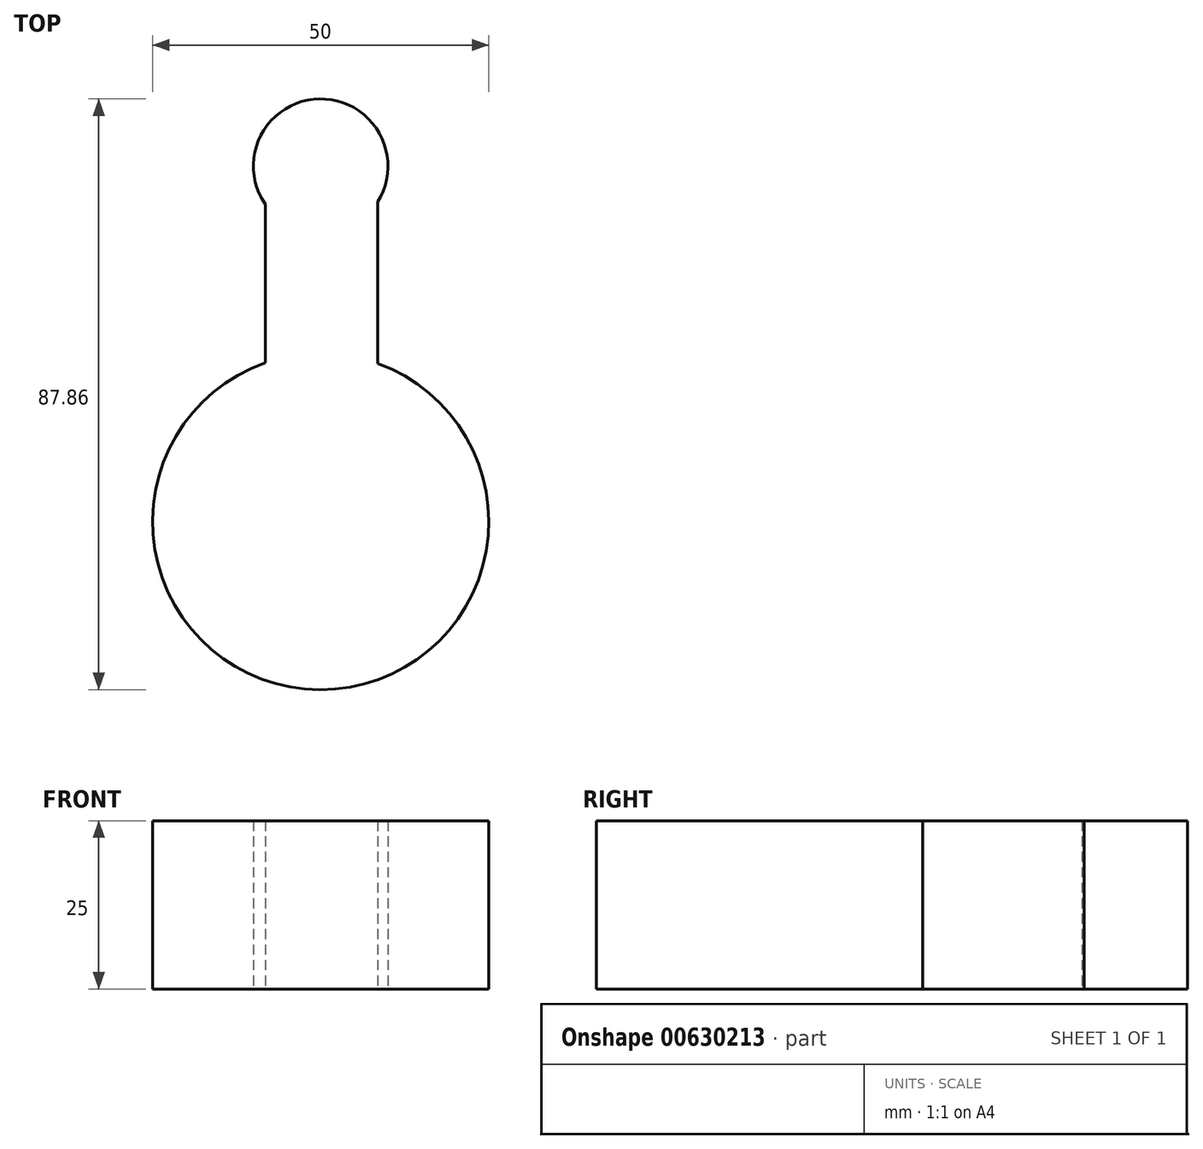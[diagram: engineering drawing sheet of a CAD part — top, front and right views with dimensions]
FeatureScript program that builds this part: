
annotation { "Feature Type Name" : "Feature", "Feature Type Description" : "" }
export const myFeature = defineFeature(function(context is Context, id is Id, definition is map)
    precondition{}
    {
        {
            var Q0;
            Q0=qCreatedBy(makeId("Top.planeOp"),FACE);
            var sketch = newSketch(context, id + "F0", { "sketchPlane" : qUnion([Q0])});
            skArc(sketch, "E0", {"start": v(-8.25, 23.6) * mm, "mid": v(-0.11, -25) * mm, "end": v(8.47, 23.52) * mm});
            skArc(sketch, "E1", {"start": v(8.47, 47.54) * mm, "mid": v(-0.2, 62.86) * mm, "end": v(-8.25, 47.21) * mm});
            skLineSegment(sketch, "E2", {"start": v(-8.25, 47.21) * mm, "end": v(-8.25, 23.6) * mm});
            skLineSegment(sketch, "E3", {"start": v(8.47, 47.54) * mm, "end": v(8.47, 23.52) * mm});
            skSolve(sketch);
        }
        {
            var Q0;
            Q0=makeQuery(id+"F0.imprint","IMPRINT",FACE,{"disambiguationData":[TD([[makeQuery(id+"F0.imprint","IMPRINT",EDGE,{"derivedFrom":sQuery(id+"F0.wireOp",EDGE,"E0")}),1.0]])]});
            var Q1;
            Q1=makeQuery(id+"F0.imprint","IMPRINT",FACE,{"disambiguationData":[TD([[makeQuery(id+"F0.imprint","IMPRINT",EDGE,{"derivedFrom":sQuery(id+"F0.wireOp",EDGE,"E1")}),1.0]])]});
            extrude(context, id + "F1", {"entities" : qUnion([Q0, Q1]), "depth" : 25 * mm, "offsetDistance" : 25 * mm});
        }
    });
